# Revit family: 873-00-001-DN1400-1500
name_source: partatom
category: Generic Models
units: mm (PartAtom-declared; Revit-internal decimal feet)

## family parameters
Always vertical = Yes
Can host rebar = No
Cut with Voids When Loaded = No
Part Type = Normal
Room Calculation Point = No
Round Connector Dimension = Use Diameter
Shared = No
Work Plane-Based = No

## types (4) — shared parameters
873-1400-00-041000 = DN1400_PN10
873-1400-00-141000 = DN1400_PN16
873-1500-00-041000 = DN1500_PN10
873-1500-00-141000 = DN1500_PN16
Angle = 22.50°
Body_Wallthicknss = 10 mm  [stored 0.0328084 ft]
Description_ = AVK DISMANTLING JOINT
Flange_thickness = 20 mm  [stored 0.0656168 ft]
Search_table = 873-00-001-DN1400-1500
URL product pages = https://www.avkvalves.com

## per-type parameters (varying)
| type | A | DN | Id(Radius) | L | T | d1 | d2 |
| DN1400_PN10 | 350 mm  [stored 1.14829 ft] | 1400 mm  [stored 4.59318 ft] | 700 mm  [stored 2.29659 ft] | 560 mm  [stored 1.83727 ft] | 39 mm  [stored 0.127953 ft] | 1590 mm  [stored 5.21654 ft] | 838 mm |
| DN1400_PN16 | 350 mm  [stored 1.14829 ft] | 1400 mm  [stored 4.59318 ft] | 700 mm  [stored 2.29659 ft] | 630 mm  [stored 2.06693 ft] | 45 mm  [stored 0.147638 ft] | 1590 mm  [stored 5.21654 ft] | 843 mm |
| DN1500_PN10 | 385 mm  [stored 1.26312 ft] | 1500 mm  [stored 4.92126 ft] | 750 mm  [stored 2.46063 ft] | 590 mm  [stored 1.9357 ft] | 39 mm  [stored 0.127953 ft] | 1700 mm  [stored 5.57743 ft] | 893 mm |
| DN1500_PN16 | 385 mm  [stored 1.26312 ft] | 1500 mm  [stored 4.92126 ft] | 750 mm  [stored 2.46063 ft] | 665 mm  [stored 2.18176 ft] | 52 mm | 1710 mm  [stored 5.61024 ft] | 910 mm |

note: [stored X ft] marks values corroborated as IEEE doubles in the binary element streams (Revit-internal decimal feet)

## geometry (parser evidence)
native form markers: Sweep x3
no freeform markers — native parametric forms only
